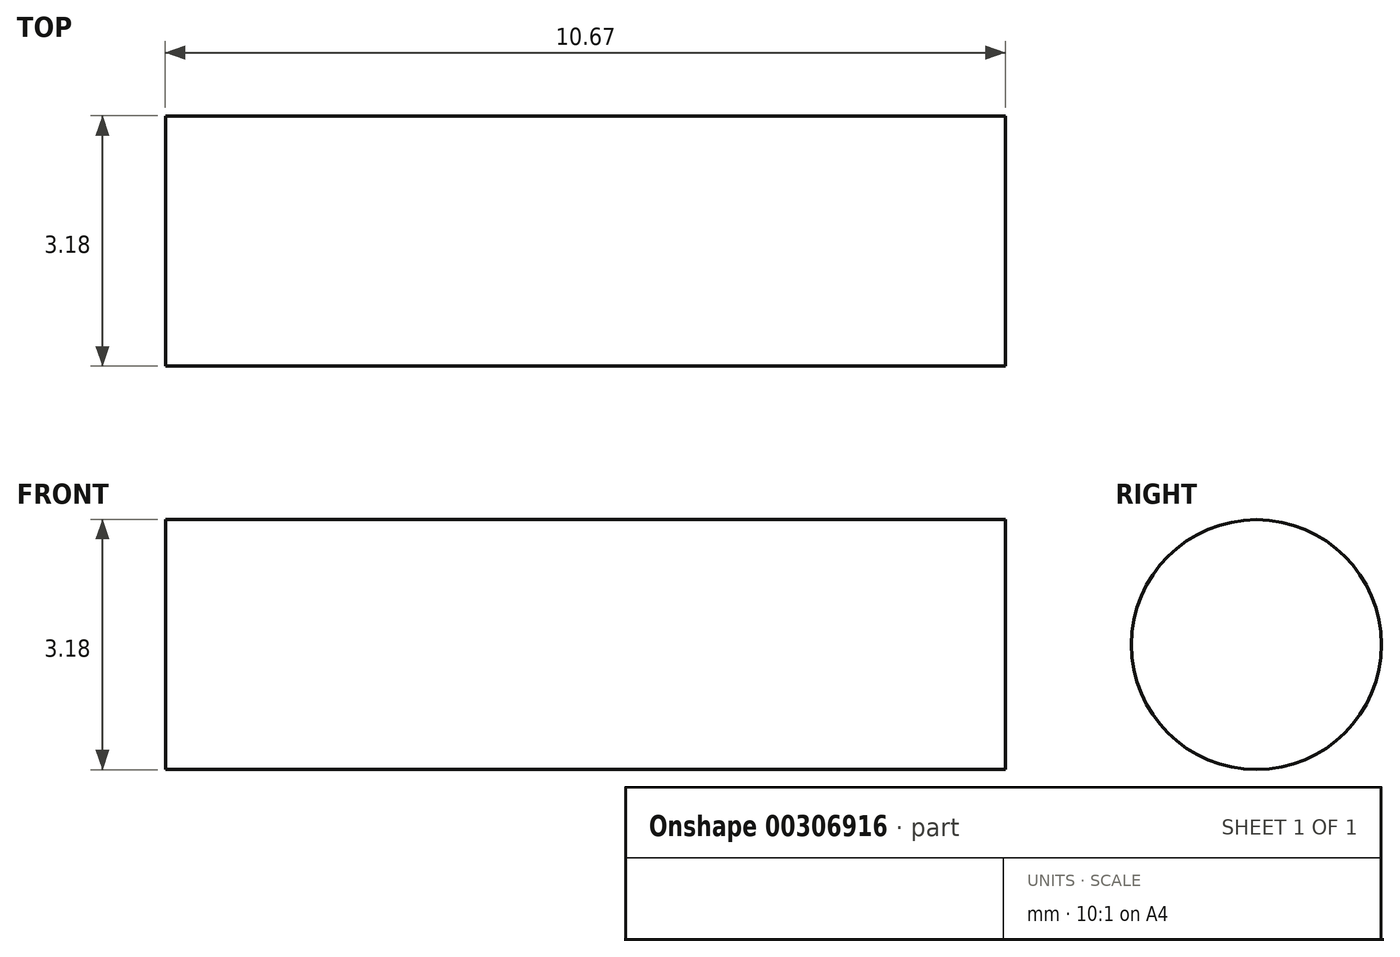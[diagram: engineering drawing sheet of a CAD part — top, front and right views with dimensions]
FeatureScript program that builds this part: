
annotation { "Feature Type Name" : "Feature", "Feature Type Description" : "" }
export const myFeature = defineFeature(function(context is Context, id is Id, definition is map)
    precondition{}
    {
        {
            var Q0;
            Q0=qCreatedBy(makeId("Right.planeOp"),FACE);
            var sketch = newSketch(context, id + "F0", { "sketchPlane" : qUnion([Q0])});
            skCircle(sketch, "E0", {"center": v(0, 0) * mm, "radius": 1.59 * mm});
            skSolve(sketch);
        }
        {
            var Q0;
            Q0=makeQuery(id+"F0.imprint","IMPRINT",FACE,{"disambiguationData":[TD([[makeQuery(id+"F0.imprint","IMPRINT",EDGE,{"derivedFrom":sQuery(id+"F0.wireOp",EDGE,"E0")}),1.0]])]});
            extrude(context, id + "F1", {"entities" : qUnion([Q0]), "oppositeDirection" : true, "depth" : 10.67 * mm});
        }
    });
